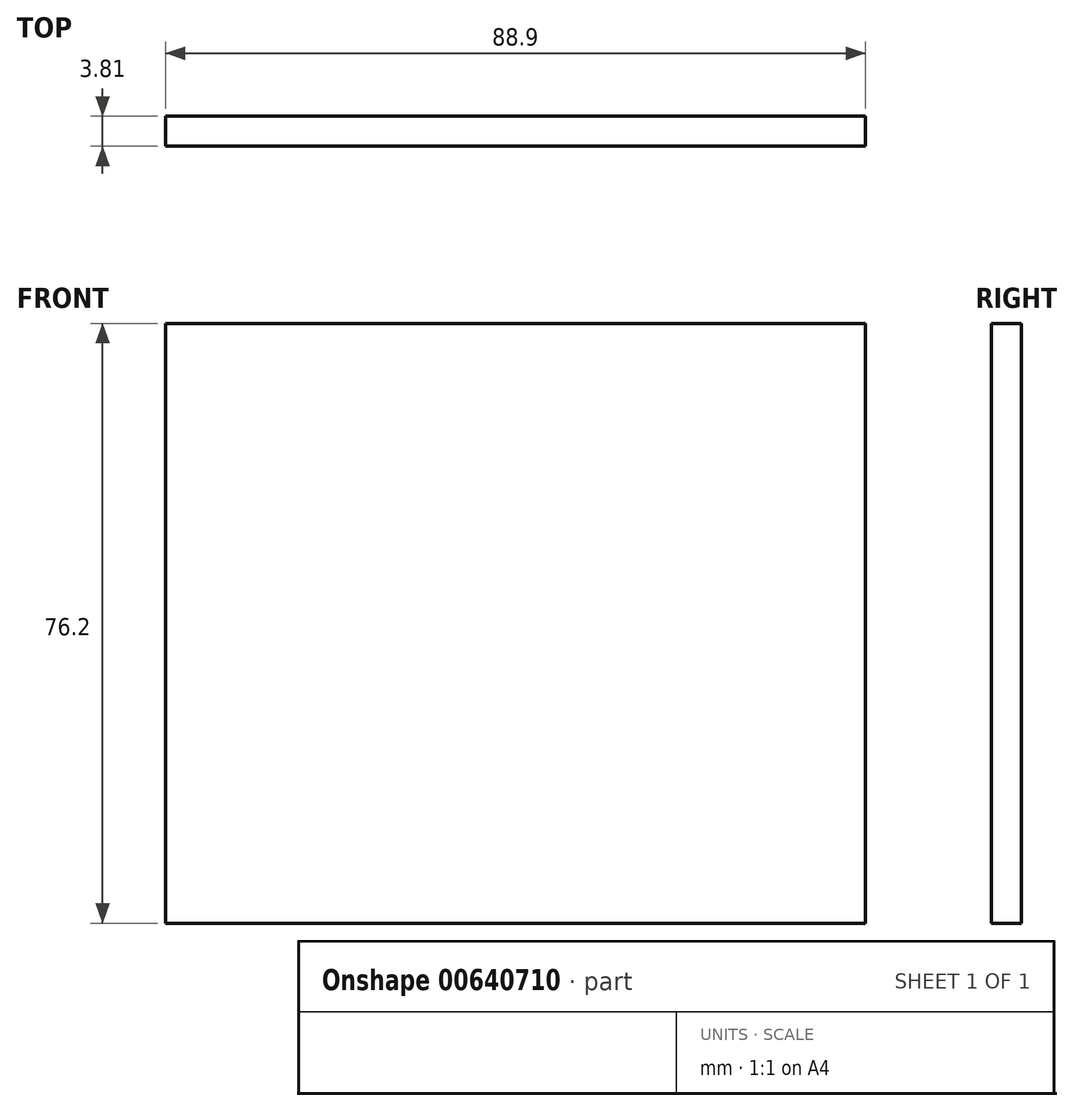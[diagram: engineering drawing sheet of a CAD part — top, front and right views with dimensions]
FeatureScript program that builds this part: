
annotation { "Feature Type Name" : "Feature", "Feature Type Description" : "" }
export const myFeature = defineFeature(function(context is Context, id is Id, definition is map)
    precondition{}
    {
        {
            var Q0;
            Q0=qCreatedBy(makeId("Front.planeOp"),FACE);
            var sketch = newSketch(context, id + "F0", { "sketchPlane" : qUnion([Q0])});
            skLineSegment(sketch, "E0", {"start": v(0, 0) * mm, "end": v(-88.9, 0) * mm});
            skLineSegment(sketch, "E1", {"start": v(-88.9, 0) * mm, "end": v(-88.9, 76.2) * mm});
            skLineSegment(sketch, "E2", {"start": v(-88.9, 76.2) * mm, "end": v(0, 76.2) * mm});
            skLineSegment(sketch, "E3", {"start": v(0, 76.2) * mm, "end": v(0, 0) * mm});
            skSolve(sketch);
        }
        {
            var Q0;
            Q0=makeQuery(id+"F0.imprint","IMPRINT",FACE,{"disambiguationData":[TD([[makeQuery(id+"F0.imprint","IMPRINT",EDGE,{"derivedFrom":sQuery(id+"F0.wireOp",EDGE,"E0")}),-1.0]])]});
            extrude(context, id + "F1", {"entities" : qUnion([Q0]), "depth" : 3.8 * mm, "offsetDistance" : 25.4 * mm});
        }
    });
